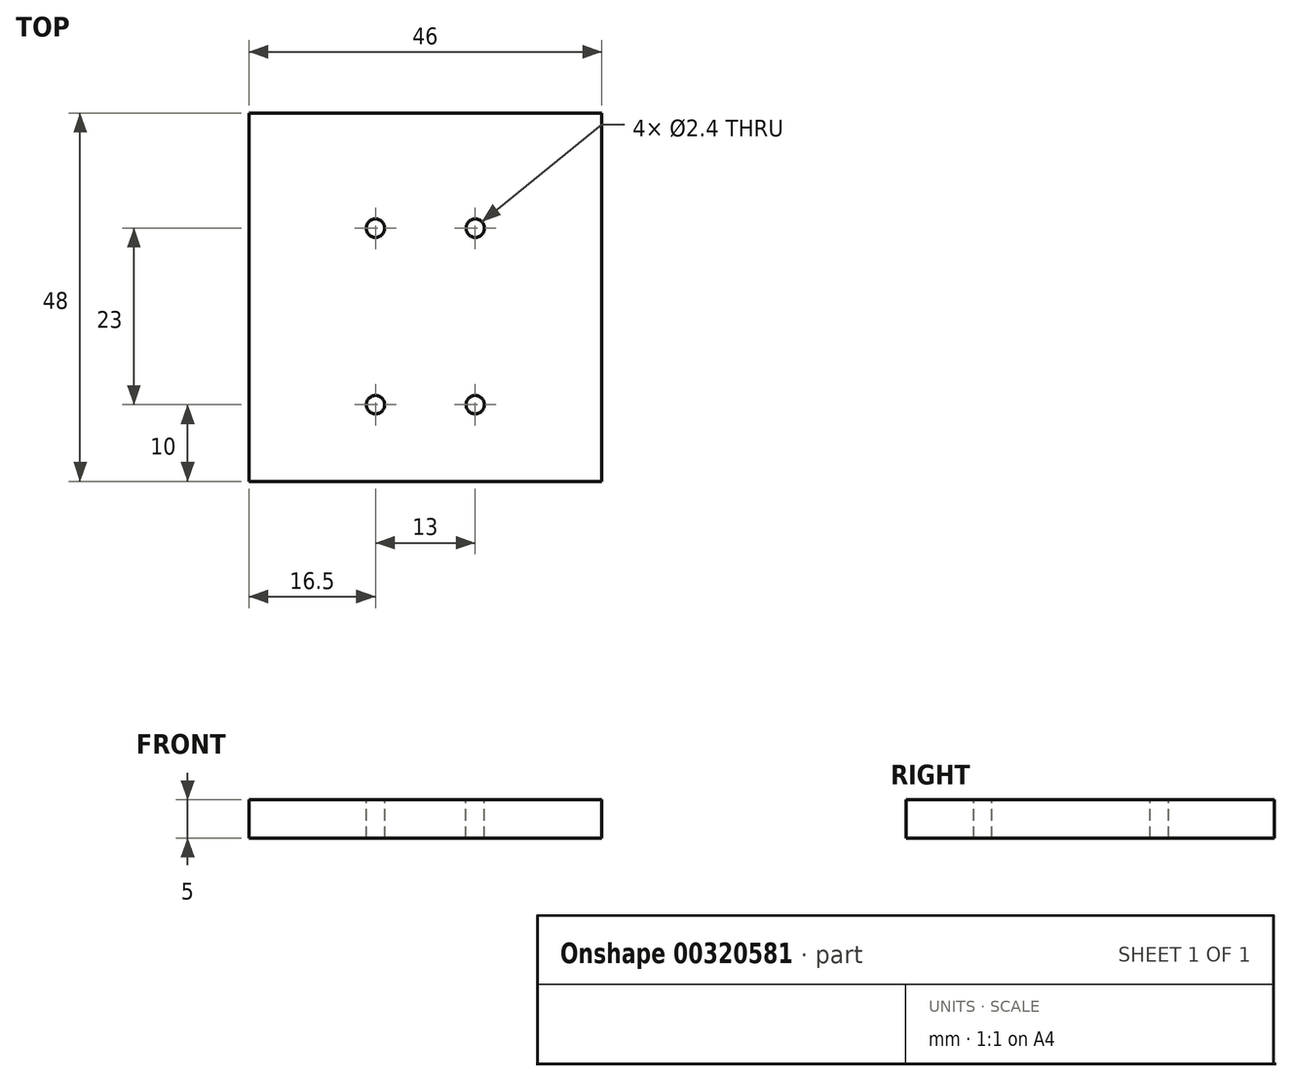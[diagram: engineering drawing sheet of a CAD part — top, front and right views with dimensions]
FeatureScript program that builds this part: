
annotation { "Feature Type Name" : "Feature", "Feature Type Description" : "" }
export const myFeature = defineFeature(function(context is Context, id is Id, definition is map)
    precondition{}
    {
        {
            var Q0;
            Q0=qCreatedBy(makeId("Top.planeOp"),FACE);
            var sketch = newSketch(context, id + "F0", { "sketchPlane" : qUnion([Q0])});
            skLineSegment(sketch, "E0.bottom", {"start": v(-23, 24) * mm, "end": v(23, 24) * mm});
            skLineSegment(sketch, "E0.top", {"start": v(-23, -24) * mm, "end": v(23, -24) * mm});
            skLineSegment(sketch, "E0.left", {"start": v(-23, 24) * mm, "end": v(-23, -24) * mm});
            skLineSegment(sketch, "E0.right", {"start": v(23, 24) * mm, "end": v(23, -24) * mm});
            skSolve(sketch);
        }
        {
            var Q0;
            Q0=makeQuery(id+"F0.imprint","IMPRINT",FACE,{"disambiguationData":[TD([[makeQuery(id+"F0.imprint","IMPRINT",EDGE,{"derivedFrom":sQuery(id+"F0.wireOp",EDGE,"E0.bottom")}),-1.0]])]});
            extrude(context, id + "F1", {"entities" : qUnion([Q0]), "endBound" : BoundingType.SYMMETRIC, "depth" : 5 * mm});
        }
        {
            var Q0;
            Q0=makeQuery(id+"F1.opExtrude","CAP_FACE",FACE,{"disambiguationData":[OSD([sQuery(id+"F0.wireOp",EDGE,"E0.bottom"),sQuery(id+"F0.wireOp",EDGE,"E0.top"),sQuery(id+"F0.wireOp",EDGE,"E0.left"),sQuery(id+"F0.wireOp",EDGE,"E0.right")])],"isStart":false});
            var sketch = newSketch(context, id + "F2", { "sketchPlane" : qUnion([Q0])});
            skPoint(sketch, "E1", {"position": v(-6.5, -14) * mm});
            skPoint(sketch, "E2", {"position": v(6.5, -14) * mm});
            skPoint(sketch, "E3", {"position": v(-6.5, 9) * mm});
            skPoint(sketch, "E4", {"position": v(6.5, 9) * mm});
            skSolve(sketch);
        }
        {
            var Q0;
            Q0=sQuery(id+"F2.wireOp",VERTEX,"E3");
            var Q1;
            Q1=sQuery(id+"F2.wireOp",VERTEX,"E4");
            var Q2;
            Q2=sQuery(id+"F2.wireOp",VERTEX,"E2");
            var Q3;
            Q3=sQuery(id+"F2.wireOp",VERTEX,"E1");
            var Q4;
            Q4=makeQuery(id+"F1.opExtrude","SWEPT_BODY",BODY,{"disambiguationData":[OSD([sQuery(id+"F0.wireOp",EDGE,"E0.bottom"),sQuery(id+"F0.wireOp",EDGE,"E0.top"),sQuery(id+"F0.wireOp",EDGE,"E0.left"),sQuery(id+"F0.wireOp",EDGE,"E0.right")])]});
            hole(context, id + "F3", {"style" : HoleStyle.SIMPLE, "endStyle" : HoleEndStyle.THROUGH, "standardTappedOrClearance" : lookupTablePath({ "standard" : "ISO", "engagement" : "75%", "pitch" : "0.6 mm", "size" : "M3", "type" : "Tapped" }), "standardBlindInLast" : lookupTablePath({ "standard" : "ISO", "engagement" : "75%", "pitch" : "0.6 mm", "size" : "M3", "type" : "Tapped" }), "holeDiameter" : 2.4 * mm, "showTappedDepth" : true, "tappedDepth" : 5 * mm, "tapClearance" : 3, "locations" : qUnion([Q0, Q1, Q2, Q3]), "scope" : qUnion([Q4])});
        }
    });
